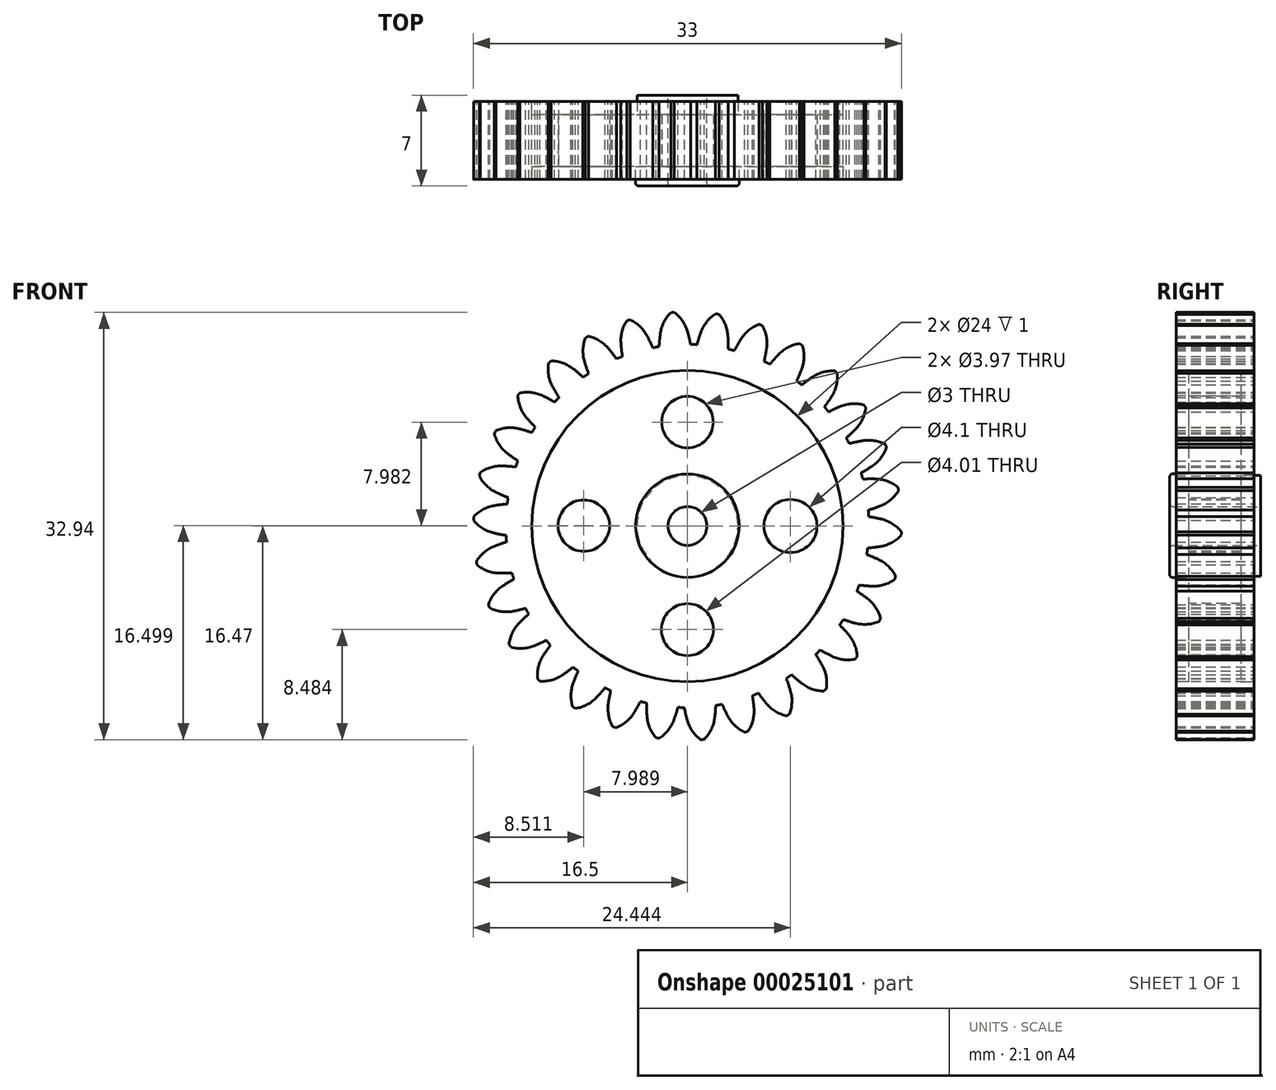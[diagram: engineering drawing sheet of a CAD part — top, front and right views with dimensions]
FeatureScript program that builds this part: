
annotation { "Feature Type Name" : "Feature", "Feature Type Description" : "" }
export const myFeature = defineFeature(function(context is Context, id is Id, definition is map)
    precondition{}
    {
        {
            var Q0;
            Q0=qCreatedBy(makeId("Front.planeOp"),FACE);
            var sketch = newSketch(context, id + "F0", { "sketchPlane" : qUnion([Q0])});
            skCircle(sketch, "E0", {"center": v(0, 0) * mm, "radius": 14 * mm});
            skCircle(sketch, "E1", {"center": v(0, 0) * mm, "radius": 15 * mm, "construction": true});
            skCircle(sketch, "E2", {"center": v(0, 0) * mm, "radius": 16.5 * mm, "construction": true});
            skLineSegment(sketch, "E3", {"start": v(0, 0) * mm, "end": v(0, 35.87) * mm, "construction": true});
            skLineSegment(sketch, "E4", {"start": v(0, 0) * mm, "end": v(-2.39, 34.16) * mm, "construction": true});
            skLineSegment(sketch, "E5", {"start": v(0, 15) * mm, "end": v(-51.18, 15) * mm, "construction": true});
            skLineSegment(sketch, "E6", {"start": v(0, 15) * mm, "end": v(-53.78, -4.57) * mm, "construction": true});
            skCircle(sketch, "E7", {"center": v(0, 15) * mm, "radius": 3.75 * mm, "construction": true});
            skCircle(sketch, "E8", {"center": v(0, 0) * mm, "radius": 14.1 * mm, "construction": true});
            skCircle(sketch, "E9", {"center": v(-3.5, 13.65) * mm, "radius": 3.75 * mm, "construction": true});
            skArc(sketch, "E10", {"start": v(0, 15) * mm, "mid": v(-0.39, 15.82) * mm, "end": v(-1.02, 16.47) * mm});
            skArc(sketch, "E11", {"start": v(0.24, 14) * mm, "mid": v(0.13, 14.5) * mm, "end": v(0, 15) * mm});
            skArc(sketch, "E12.MirrorCS", {"start": v(-2.09, 14.85) * mm, "mid": v(-1.82, 15.72) * mm, "end": v(-1.28, 16.45) * mm});
            skArc(sketch, "E13.MirrorCS", {"start": v(-2.18, 13.83) * mm, "mid": v(-2.15, 14.34) * mm, "end": v(-2.09, 14.85) * mm});
            skArc(sketch, "E14", {"start": v(-1.02, 16.47) * mm, "mid": v(-1.15, 16.46) * mm, "end": v(-1.28, 16.45) * mm});
            skCircle(sketch, "E15", {"center": v(0, 0) * mm, "radius": 1.5 * mm});
            skCircle(sketch, "E16", {"center": v(0, 0) * mm, "radius": 4 * mm});
            skCircle(sketch, "E17", {"center": v(0, 0) * mm, "radius": 12 * mm});
            skCircle(sketch, "E18", {"center": v(0, -8) * mm, "radius": 2 * mm});
            skSolve(sketch);
        }
        {
            var Q0;
            Q0=makeQuery(id+"F0.imprint","IMPRINT",FACE,{"disambiguationData":[TD([[makeQuery(id+"F0.imprint","IMPRINT",EDGE,{"derivedFrom":sQuery(id+"F0.wireOp",EDGE,"E16")}),-1.0]])]});
            var Q1;
            Q1=makeQuery(id+"F0.imprint","IMPRINT",FACE,{"disambiguationData":[TD([[makeQuery(id+"F0.imprint","IMPRINT",EDGE,{"derivedFrom":sQuery(id+"F0.wireOp",EDGE,"E17")}),-1.0]])]});
            var Q2;
            Q2=makeQuery(id+"F0.imprint","IMPRINT",FACE,{"disambiguationData":[TD([[makeQuery(id+"F0.imprint","IMPRINT",EDGE,{"derivedFrom":sQuery(id+"F0.wireOp",EDGE,"E10")}),1.0]])]});
            var Q3;
            Q3=makeQuery(id+"F0.imprint","IMPRINT",FACE,{"disambiguationData":[TD([[makeQuery(id+"F0.imprint","IMPRINT",EDGE,{"derivedFrom":sQuery(id+"F0.wireOp",EDGE,"E15")}),-1.0]])]});
            var Q4;
            Q4=makeQuery(id+"F0.imprint","IMPRINT",FACE,{"disambiguationData":[TD([[makeQuery(id+"F0.imprint","IMPRINT",EDGE,{"derivedFrom":sQuery(id+"F0.wireOp",EDGE,"E18")}),1.0]])]});
            var Q5;
            Q5=makeQuery(id+"F0.imprint","IMPRINT",FACE,{"disambiguationData":[TD([[makeQuery(id+"F0.imprint","IMPRINT",EDGE,{"derivedFrom":sQuery(id+"F0.wireOp",EDGE,"E15")}),1.0]])]});
            extrude(context, id + "F1", {"entities" : qUnion([Q0, Q1, Q2, Q3, Q4, Q5]), "depth" : 6 * mm});
        }
        {
            var Q0;
            Q0=makeQuery(id+"F1.opExtrude","SWEPT_BODY",BODY,{"disambiguationData":[OSD([sQuery(id+"F0.wireOp",EDGE,"E0"),sQuery(id+"F0.wireOp",EDGE,"E10"),sQuery(id+"F0.wireOp",EDGE,"E11"),sQuery(id+"F0.wireOp",EDGE,"E12.MirrorCS"),sQuery(id+"F0.wireOp",EDGE,"E13.MirrorCS"),sQuery(id+"F0.wireOp",EDGE,"E14")])]});
            var Q1;
            Q1=makeQuery(id+"F1.opExtrude","SWEPT_FACE",FACE,{"disambiguationData":[OSD([sQuery(id+"F0.wireOp",EDGE,"E0")])]});
            circularPattern(context, id + "F2", {"entities" : qUnion([Q0]), "axis" : qUnion([Q1]), "angle" : 12 * degree, "instanceCount" : 30});
        }
        {
            var Q0;
            Q0=makeQuery(id+"F1.opExtrude","CAP_FACE",FACE,{"disambiguationData":[OSD([sQuery(id+"F0.wireOp",EDGE,"E0"),sQuery(id+"F0.wireOp",EDGE,"E10"),sQuery(id+"F0.wireOp",EDGE,"E11"),sQuery(id+"F0.wireOp",EDGE,"E12.MirrorCS"),sQuery(id+"F0.wireOp",EDGE,"E13.MirrorCS"),sQuery(id+"F0.wireOp",EDGE,"E14")])],"isStart":false});
            var sketch = newSketch(context, id + "F3", { "sketchPlane" : qUnion([Q0])});
            skCircle(sketch, "E19", {"center": v(0, 0) * mm, "radius": 12 * mm});
            skSolve(sketch);
        }
        {
            var Q0;
            Q0=makeQuery(id+"F3.imprint","IMPRINT",FACE,{"disambiguationData":[TD([[makeQuery(id+"F3.imprint","IMPRINT",EDGE,{"derivedFrom":sQuery(id+"F3.wireOp",EDGE,"E19")}),1.0]])]});
            extrude(context, id + "F4", {"entities" : qUnion([Q0]), "operationType" : NewBodyOperationType.REMOVE, "oppositeDirection" : true, "depth" : 1 * mm});
        }
        {
            var Q0;
            Q0=makeQuery(id+"F2.opPattern","COPY",FACE,{"derivedFrom":makeQuery(id+"F1.opExtrude","CAP_FACE",FACE,{"disambiguationData":[OSD([sQuery(id+"F0.wireOp",EDGE,"E0"),sQuery(id+"F0.wireOp",EDGE,"E10"),sQuery(id+"F0.wireOp",EDGE,"E11"),sQuery(id+"F0.wireOp",EDGE,"E12.MirrorCS"),sQuery(id+"F0.wireOp",EDGE,"E13.MirrorCS"),sQuery(id+"F0.wireOp",EDGE,"E14")])],"isStart":true}),"instanceName":"7"});
            var sketch = newSketch(context, id + "F5", { "sketchPlane" : qUnion([Q0])});
            skCircle(sketch, "E20", {"center": v(0, 0) * mm, "radius": 12 * mm});
            skSolve(sketch);
        }
        {
            var Q0;
            Q0=makeQuery(id+"F5.imprint","IMPRINT",FACE,{"disambiguationData":[TD([[makeQuery(id+"F5.imprint","IMPRINT",EDGE,{"derivedFrom":sQuery(id+"F5.wireOp",EDGE,"E20")}),1.0]])]});
            extrude(context, id + "F6", {"entities" : qUnion([Q0]), "operationType" : NewBodyOperationType.REMOVE, "oppositeDirection" : true, "depth" : 1 * mm});
        }
        {
            var Q0;
            Q0=makeQuery(id+"F4.boolean.opBoolean","COPY",FACE,{"disambiguationData":[OD(20.0)],"derivedFrom":makeQuery(id+"F4.opExtrude","CAP_FACE",FACE,{"disambiguationData":[OSD([sQuery(id+"F3.wireOp",EDGE,"E19")])],"isStart":false})});
            var sketch = newSketch(context, id + "F7", { "sketchPlane" : qUnion([Q0])});
            skCircle(sketch, "E21", {"center": v(0, 0) * mm, "radius": 1.5 * mm});
            skCircle(sketch, "E22", {"center": v(0, -7.97) * mm, "radius": 2 * mm});
            skCircle(sketch, "E23", {"center": v(0, 0.03) * mm, "radius": 4 * mm});
            skSolve(sketch);
        }
        {
            var Q0;
            Q0=makeQuery(id+"F7.imprint","IMPRINT",FACE,{"disambiguationData":[TD([[makeQuery(id+"F7.imprint","IMPRINT",EDGE,{"derivedFrom":sQuery(id+"F7.wireOp",EDGE,"E21")}),-1.0]])]});
            extrude(context, id + "F8", {"entities" : qUnion([Q0]), "operationType" : NewBodyOperationType.ADD, "depth" : 1.5 * mm});
        }
        {
            var Q0;
            Q0=makeQuery(id+"F8.opExtrude","CAP_FACE",FACE,{"disambiguationData":[OSD([sQuery(id+"F7.wireOp",EDGE,"E21"),sQuery(id+"F7.wireOp",EDGE,"E23")])],"isStart":false});
            var Q1;
            Q1=makeQuery(id+"F8.opExtrude","CAP_EDGE",EDGE,{"disambiguationData":[OSD([sQuery(id+"F7.wireOp",EDGE,"E23")])],"isStart":false});
            fillet(context, id + "F9", {"entities" : qUnion([Q0, Q1]), "radius" : 0.24 * mm, "tangentPropagation" : true, "allowEdgeOverflow" : false});
        }
        {
            var Q0;
            Q0=makeQuery(id+"F8.boolean.opBoolean","SPLIT",FACE,{"disambiguationData":[TD([makeQuery(id+"F8.opExtrude","SWEPT_FACE",FACE,{"disambiguationData":[OSD([sQuery(id+"F7.wireOp",EDGE,"E21")])]})])],"derivedFrom":makeQuery(id+"F4.boolean.opBoolean","COPY",FACE,{"disambiguationData":[OD(0.0)],"derivedFrom":makeQuery(id+"F4.opExtrude","CAP_FACE",FACE,{"disambiguationData":[OSD([sQuery(id+"F3.wireOp",EDGE,"E19")])],"isStart":false})})});
            extrude(context, id + "F10", {"entities" : qUnion([Q0]), "operationType" : NewBodyOperationType.REMOVE, "oppositeDirection" : true, "depth" : 25.4 * mm});
        }
        {
            var Q0;
            {var subQ0=sQuery(id+"F3.wireOp",EDGE,"E19");Q0=makeQuery(id+"F8.boolean.opBoolean","SPLIT",FACE,{"disambiguationData":[TD([makeQuery(id+"F4.boolean.opBoolean","COPY",FACE,{"disambiguationData":[OD(0.0)],"derivedFrom":makeQuery(id+"F4.opExtrude","SWEPT_FACE",FACE,{"disambiguationData":[OSD([subQ0])]})})])],"derivedFrom":makeQuery(id+"F4.boolean.opBoolean","COPY",FACE,{"disambiguationData":[OD(0.0)],"derivedFrom":makeQuery(id+"F4.opExtrude","CAP_FACE",FACE,{"disambiguationData":[OSD([subQ0])],"isStart":false})})});}
            var sketch = newSketch(context, id + "F11", { "sketchPlane" : qUnion([Q0])});
            skCircle(sketch, "E24", {"center": v(0, 8.01) * mm, "radius": 1.98 * mm});
            skLineSegment(sketch, "E25", {"start": v(0, 0) * mm, "end": v(0, 8.01) * mm, "construction": true});
            skCircle(sketch, "E26", {"center": v(7.94, 0) * mm, "radius": 2.05 * mm});
            skCircle(sketch, "E27", {"center": v(0, -7.99) * mm, "radius": 2 * mm});
            skCircle(sketch, "E28", {"center": v(-7.99, 0.03) * mm, "radius": 1.98 * mm});
            skLineSegment(sketch, "E29", {"start": v(0, 0) * mm, "end": v(0, -12) * mm, "construction": true});
            skLineSegment(sketch, "E30", {"start": v(0, 0) * mm, "end": v(-12, 0) * mm, "construction": true});
            skLineSegment(sketch, "E31", {"start": v(0, 0) * mm, "end": v(12, 0) * mm, "construction": true});
            skSolve(sketch);
        }
        {
            var Q0;
            Q0=makeQuery(id+"F11.imprint","IMPRINT",FACE,{"disambiguationData":[TD([[makeQuery(id+"F11.imprint","IMPRINT",EDGE,{"derivedFrom":sQuery(id+"F11.wireOp",EDGE,"E24")}),1.0]])]});
            var Q1;
            Q1=makeQuery(id+"F11.imprint","IMPRINT",FACE,{"disambiguationData":[TD([[makeQuery(id+"F11.imprint","IMPRINT",EDGE,{"derivedFrom":sQuery(id+"F11.wireOp",EDGE,"E28")}),1.0]])]});
            var Q2;
            Q2=makeQuery(id+"F11.imprint","IMPRINT",FACE,{"disambiguationData":[TD([[makeQuery(id+"F11.imprint","IMPRINT",EDGE,{"derivedFrom":sQuery(id+"F11.wireOp",EDGE,"E27")}),1.0]])]});
            var Q3;
            Q3=makeQuery(id+"F11.imprint","IMPRINT",FACE,{"disambiguationData":[TD([[makeQuery(id+"F11.imprint","IMPRINT",EDGE,{"derivedFrom":sQuery(id+"F11.wireOp",EDGE,"E26")}),1.0]])]});
            extrude(context, id + "F12", {"entities" : qUnion([Q0, Q1, Q2, Q3]), "operationType" : NewBodyOperationType.REMOVE, "oppositeDirection" : true, "depth" : 25.4 * mm});
        }
        {
            var Q0;
            Q0=makeQuery(id+"F6.boolean.opBoolean","COPY",FACE,{"disambiguationData":[OD(0.0)],"derivedFrom":makeQuery(id+"F6.opExtrude","CAP_FACE",FACE,{"disambiguationData":[OSD([sQuery(id+"F5.wireOp",EDGE,"E20")])],"isStart":false})});
            var sketch = newSketch(context, id + "F13", { "sketchPlane" : qUnion([Q0])});
            skCircle(sketch, "E32", {"center": v(0, 0) * mm, "radius": 3.89 * mm});
            skSolve(sketch);
        }
        {
            var Q0;
            Q0=makeQuery(id+"F13.imprint","IMPRINT",FACE,{"disambiguationData":[TD([[makeQuery(id+"F13.imprint","IMPRINT",EDGE,{"derivedFrom":sQuery(id+"F13.wireOp",EDGE,"E32")}),1.0]])]});
            extrude(context, id + "F14", {"entities" : qUnion([Q0]), "operationType" : NewBodyOperationType.ADD, "depth" : 1.5 * mm});
        }
    });
